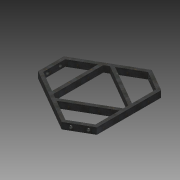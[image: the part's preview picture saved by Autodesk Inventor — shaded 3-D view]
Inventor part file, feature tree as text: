
AUTODESK INVENTOR PART (.ipt)
format: ipt  version: 2015 SP1 (Build 190203100, 203)  size: 154,624 bytes
history: native  units: in
note: dims shown in document units (in); Inventor stores cm internally (conversion verified against a paired STEP export)
features: extrude x4, sketch x4, projected_geometry x3
ambient origin geometry x8: Origin, YZ Plane, XZ Plane, XY Plane, X Axis, Y Axis, Z Axis, Center Point
bodies: Solid1 (feature_tree)
feature tree (11):
  extrude  "Extrusion1"  Depth=20.0in
  extrude  "Extrusion2"  Depth=15.5in
  extrude  "Extrusion3"  Depth=2.0in TaperAngle=0.0deg
  extrude  "Extrusion4"  Depth=2.0in
  sketch  "Sketch1"  dims[d0=8.0in d6=20.0in]
  sketch  "Sketch2"  dims[d14=15.5in d16=15.5in]
  projected_geometry  "Projected Loop1"
  sketch  "Sketch3"  dims[d17=15.5in d21=2.0in d22=0.0in]
  projected_geometry  "Projected Loop2"
  sketch  "Sketch4"  dims[d23=2.0in d24=2.0in d25=1.0in d26=1.0in d27=1.0in d28=0.0in d29=2.0in d30=2.0in d31=1.0in d32=1.0in d33=1.0in d34=0.0in d35=2.0in d36=2.0in d37=1.0in d38=1.0in d39=1.0in d40=0.0in]
  projected_geometry  "Projected Loop3"
